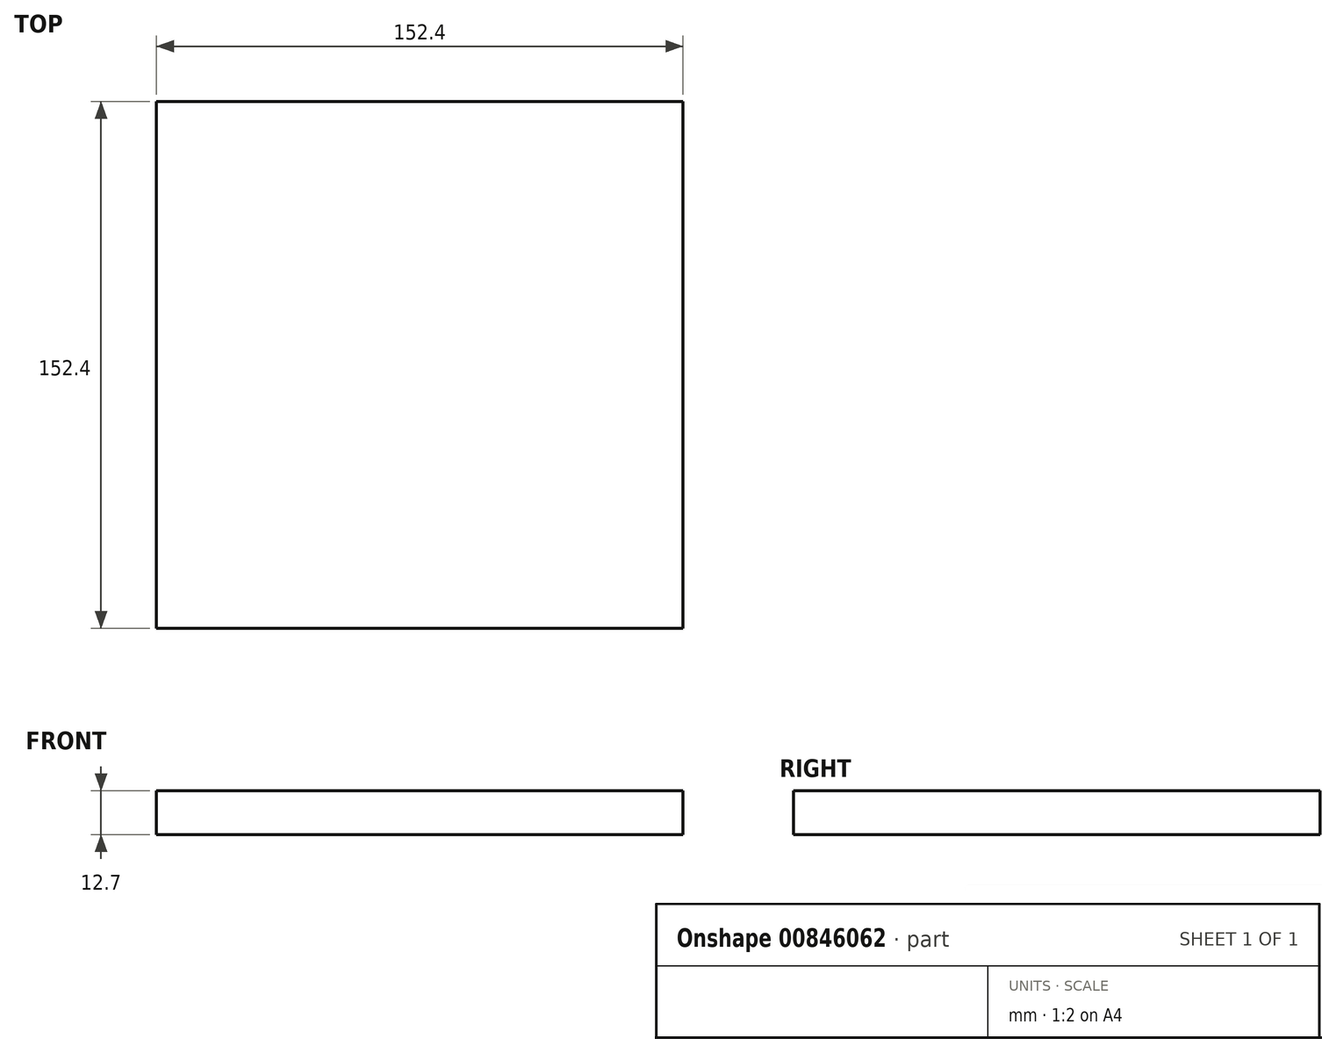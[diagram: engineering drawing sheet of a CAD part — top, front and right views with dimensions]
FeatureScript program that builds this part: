
annotation { "Feature Type Name" : "Feature", "Feature Type Description" : "" }
export const myFeature = defineFeature(function(context is Context, id is Id, definition is map)
    precondition{}
    {
        {
            var Q0;
            Q0=qCreatedBy(makeId("Top.planeOp"),FACE);
            var sketch = newSketch(context, id + "F0", { "sketchPlane" : qUnion([Q0])});
            skLineSegment(sketch, "E0.bottom", {"start": v(76.2, -76.2) * mm, "end": v(-76.2, -76.2) * mm});
            skLineSegment(sketch, "E0.top", {"start": v(76.2, 76.2) * mm, "end": v(-76.2, 76.2) * mm});
            skLineSegment(sketch, "E0.left", {"start": v(76.2, -76.2) * mm, "end": v(76.2, 76.2) * mm});
            skLineSegment(sketch, "E0.right", {"start": v(-76.2, -76.2) * mm, "end": v(-76.2, 76.2) * mm});
            skPoint(sketch, "E0.middle", {"position": v(0, 0) * mm});
            skSolve(sketch);
        }
        {
            var Q0;
            Q0 = qSketchRegion(id + "F0", true);
            extrude(context, id + "F1", {"entities" : qUnion([Q0]), "depth" : 12.7 * mm, "offsetDistance" : 25.4 * mm});
        }
    });
